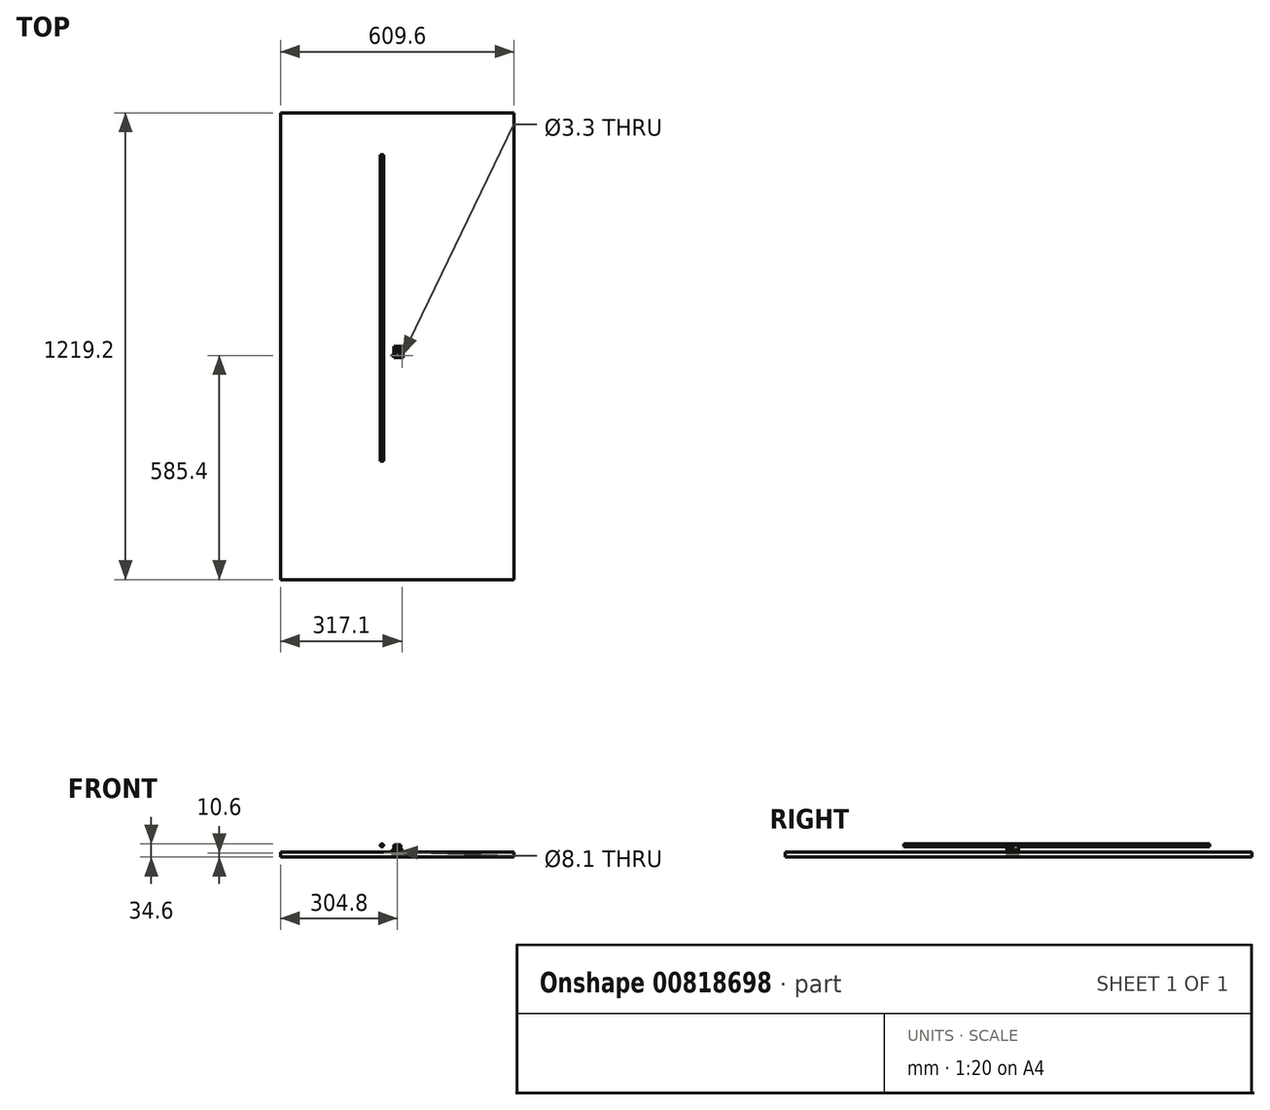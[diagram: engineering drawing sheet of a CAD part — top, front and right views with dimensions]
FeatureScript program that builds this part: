
annotation { "Feature Type Name" : "Feature", "Feature Type Description" : "" }
export const myFeature = defineFeature(function(context is Context, id is Id, definition is map)
    precondition{}
    {
        {
            var Q0;
            Q0=qCreatedBy(makeId("Front.planeOp"),FACE);
            var sketch = newSketch(context, id + "F0", { "sketchPlane" : qUnion([Q0])});
            skLineSegment(sketch, "E0", {"start": v(-20.5, 0) * mm, "end": v(-20.5, 6) * mm});
            skLineSegment(sketch, "E1", {"start": v(-20.5, 6) * mm, "end": v(-8.95, 6) * mm});
            skLineSegment(sketch, "E2", {"start": v(-8.95, 6) * mm, "end": v(-8.95, 32) * mm});
            skLineSegment(sketch, "E3", {"start": v(-8.95, 32) * mm, "end": v(-0.65, 32) * mm});
            skLineSegment(sketch, "E4", {"start": v(-20.5, 0) * mm, "end": v(0, 0) * mm});
            skLineSegment(sketch, "E5.MirrorCS", {"start": v(8.95, 32) * mm, "end": v(0.65, 32) * mm});
            skLineSegment(sketch, "E6.MirrorCS", {"start": v(8.95, 6) * mm, "end": v(8.95, 32) * mm});
            skLineSegment(sketch, "E7.MirrorCS", {"start": v(20.5, 6) * mm, "end": v(8.95, 6) * mm});
            skLineSegment(sketch, "E8.MirrorCS", {"start": v(20.5, 0) * mm, "end": v(20.5, 6) * mm});
            skLineSegment(sketch, "E9.MirrorCS", {"start": v(20.5, 0) * mm, "end": v(0, 0) * mm});
            skArc(sketch, "E10", {"start": v(-0.65, 23.05) * mm, "mid": v(0, 14.9) * mm, "end": v(0.65, 23.05) * mm});
            skLineSegment(sketch, "E11", {"start": v(-0.65, 32) * mm, "end": v(-0.65, 23.05) * mm});
            skLineSegment(sketch, "E12.MirrorCS", {"start": v(0.65, 32) * mm, "end": v(0.65, 23.05) * mm});
            skPoint(sketch, "E13.orphan", {"position": v(0, 32) * mm});
            skSolve(sketch);
        }
        {
            var Q0;
            Q0=makeQuery(id+"F0.imprint","IMPRINT",FACE,{"disambiguationData":[TD([[makeQuery(id+"F0.imprint","IMPRINT",EDGE,{"derivedFrom":sQuery(id+"F0.wireOp",EDGE,"E0")}),-1.0]])]});
            extrude(context, id + "F1", {"entities" : qUnion([Q0]), "depth" : 14.5 * mm, "offsetDistance" : 25 * mm});
        }
        {
            var Q0;
            Q0=makeQuery(id+"F1.opExtrude","SWEPT_FACE",FACE,{"disambiguationData":[OSD([sQuery(id+"F0.wireOp",EDGE,"E4"),sQuery(id+"F0.wireOp",EDGE,"E9.MirrorCS")])]});
            var sketch = newSketch(context, id + "F2", { "sketchPlane" : qUnion([Q0])});
            skLineSegment(sketch, "E14", {"start": v(-20.5, 7.25) * mm, "end": v(20.5, 7.25) * mm, "construction": true});
            skCircle(sketch, "E15", {"center": v(-16, 7.25) * mm, "radius": 2.7 * mm});
            skCircle(sketch, "E16.MirrorC", {"center": v(16, 7.25) * mm, "radius": 2.7 * mm});
            skSolve(sketch);
        }
        {
            var Q0;
            Q0=makeQuery(id+"F2.imprint","IMPRINT",FACE,{"disambiguationData":[TD([[makeQuery(id+"F2.imprint","IMPRINT",EDGE,{"derivedFrom":sQuery(id+"F2.wireOp",EDGE,"E15")}),1.0]])]});
            var Q1;
            Q1=makeQuery(id+"F2.imprint","IMPRINT",FACE,{"disambiguationData":[TD([[makeQuery(id+"F2.imprint","IMPRINT",EDGE,{"derivedFrom":sQuery(id+"F2.wireOp",EDGE,"E16.MirrorC")}),-1.0]])]});
            var Q2;
            Q2=makeQuery(id+"F1.opExtrude","SWEPT_FACE",FACE,{"disambiguationData":[OSD([sQuery(id+"F0.wireOp",EDGE,"E1")])]});
            extrude(context, id + "F3", {"entities" : qUnion([Q0, Q1]), "operationType" : NewBodyOperationType.REMOVE, "endBound" : BoundingType.UP_TO_SURFACE, "oppositeDirection" : true, "depth" : 25 * mm, "endBoundEntityFace" : qUnion([Q2]), "offsetDistance" : 25 * mm});
        }
        {
            var Q0;
            Q0=qCreatedBy(makeId("Front.planeOp"),FACE);
            var sketch = newSketch(context, id + "F4", { "sketchPlane" : qUnion([Q0])});
            skCircle(sketch, "E17", {"center": v(-40, 30) * mm, "radius": 4 * mm});
            skSolve(sketch);
        }
        {
            var Q0;
            Q0=makeQuery(id+"F4.imprint","IMPRINT",FACE,{"disambiguationData":[TD([[makeQuery(id+"F4.imprint","IMPRINT",EDGE,{"derivedFrom":sQuery(id+"F4.wireOp",EDGE,"E17")}),1.0]])]});
            extrude(context, id + "F5", {"entities" : qUnion([Q0]), "depth" : 300 * mm, "offsetDistance" : 25 * mm});
        }
        {
            var Q0;
            Q0=makeQuery(id+"F4.imprint","IMPRINT",FACE,{"disambiguationData":[TD([[makeQuery(id+"F4.imprint","IMPRINT",EDGE,{"derivedFrom":sQuery(id+"F4.wireOp",EDGE,"E17")}),1.0]])]});
            extrude(context, id + "F6", {"entities" : qUnion([Q0]), "oppositeDirection" : true, "depth" : 500 * mm, "offsetDistance" : 25 * mm});
        }
        {
            var Q0;
            Q0=qCreatedBy(makeId("Front.planeOp"),FACE);
            var sketch = newSketch(context, id + "F7", { "sketchPlane" : qUnion([Q0])});
            skLineSegment(sketch, "E18", {"start": v(0, 0) * mm, "end": v(-6.5, 0) * mm});
            skLineSegment(sketch, "E19", {"start": v(-6.5, 0) * mm, "end": v(-6.5, -0.6) * mm});
            skLineSegment(sketch, "E20", {"start": v(-6.5, -0.6) * mm, "end": v(-17, -0.6) * mm});
            skLineSegment(sketch, "E21", {"start": v(-17, -0.6) * mm, "end": v(-17, 6) * mm});
            skLineSegment(sketch, "E22", {"start": v(-17, 6) * mm, "end": v(-15.5, 7.4) * mm});
            skLineSegment(sketch, "E23", {"start": v(-15.5, 7.4) * mm, "end": v(-15.5, 17.4) * mm});
            skLineSegment(sketch, "E24", {"start": v(-5, 21) * mm, "end": v(0, 21) * mm});
            skCircle(sketch, "E25", {"center": v(0, 10) * mm, "radius": 4.05 * mm});
            skCircle(sketch, "E26", {"center": v(0, 10) * mm, "radius": 7.5 * mm});
            skLineSegment(sketch, "E27", {"start": v(-15.5, 17.4) * mm, "end": v(-8.5, 17.4) * mm});
            skLineSegment(sketch, "E28", {"start": v(-8.5, 17.4) * mm, "end": v(-5, 21) * mm});
            skLineSegment(sketch, "E29.MirrorCS", {"start": v(5, 21) * mm, "end": v(0, 21) * mm});
            skLineSegment(sketch, "E30.MirrorCS", {"start": v(8.5, 17.4) * mm, "end": v(5, 21) * mm});
            skLineSegment(sketch, "E31.MirrorCS", {"start": v(15.5, 17.4) * mm, "end": v(8.5, 17.4) * mm});
            skLineSegment(sketch, "E32.MirrorCS", {"start": v(15.5, 7.4) * mm, "end": v(15.5, 17.4) * mm});
            skLineSegment(sketch, "E33.MirrorCS", {"start": v(17, 6) * mm, "end": v(15.5, 7.4) * mm});
            skLineSegment(sketch, "E34.MirrorCS", {"start": v(17, -0.6) * mm, "end": v(17, 6) * mm});
            skLineSegment(sketch, "E35.MirrorCS", {"start": v(6.5, -0.6) * mm, "end": v(17, -0.6) * mm});
            skLineSegment(sketch, "E36.MirrorCS", {"start": v(0, 0) * mm, "end": v(6.5, 0) * mm});
            skLineSegment(sketch, "E37.MirrorCS", {"start": v(6.5, 0) * mm, "end": v(6.5, -0.6) * mm});
            skSolve(sketch);
        }
        {
            var Q0;
            Q0=makeQuery(id+"F7.imprint","IMPRINT",FACE,{"disambiguationData":[TD([[makeQuery(id+"F7.imprint","IMPRINT",EDGE,{"derivedFrom":sQuery(id+"F7.wireOp",EDGE,"E18")}),-1.0]])]});
            var Q1;
            Q1=makeQuery(id+"F7.imprint","IMPRINT",FACE,{"disambiguationData":[TD([[makeQuery(id+"F7.imprint","IMPRINT",EDGE,{"derivedFrom":sQuery(id+"F7.wireOp",EDGE,"E25")}),-1.0]])]});
            extrude(context, id + "F8", {"entities" : qUnion([Q0, Q1]), "depth" : 30 * mm, "offsetDistance" : 25 * mm});
        }
        {
            var Q0;
            Q0=makeQuery(id+"F8.opExtrude","SWEPT_FACE",FACE,{"disambiguationData":[OSD([sQuery(id+"F7.wireOp",EDGE,"E20")])]});
            var sketch = newSketch(context, id + "F9", { "sketchPlane" : qUnion([Q0])});
            skLineSegment(sketch, "E38", {"start": v(-17, 5.8) * mm, "end": v(17, 5.8) * mm, "construction": true});
            skCircle(sketch, "E39", {"center": v(-12.3, 5.8) * mm, "radius": 1.65 * mm});
            skLineSegment(sketch, "E40", {"start": v(-17, 15) * mm, "end": v(17, 15) * mm, "construction": true});
            skCircle(sketch, "E41.MirrorC", {"center": v(-12.3, 24.2) * mm, "radius": 1.65 * mm});
            skCircle(sketch, "E42.MirrorC", {"center": v(12.3, 24.2) * mm, "radius": 1.65 * mm});
            skCircle(sketch, "E43.MirrorC", {"center": v(12.3, 5.8) * mm, "radius": 1.65 * mm});
            skLineSegment(sketch, "E44", {"start": v(-17, 30) * mm, "end": v(17, 0) * mm, "construction": true});
            skLineSegment(sketch, "E45", {"start": v(-17, 0) * mm, "end": v(17, 30) * mm, "construction": true});
            skPoint(sketch, "E46.0", {"position": v(17, 0) * mm});
            skPoint(sketch, "E47", {"position": v(0, 15) * mm});
            skSolve(sketch);
        }
        {
            var Q0;
            Q0=makeQuery(id+"F9.imprint","IMPRINT",FACE,{"disambiguationData":[TD([[makeQuery(id+"F9.imprint","IMPRINT",EDGE,{"derivedFrom":sQuery(id+"F9.wireOp",EDGE,"E41.MirrorC")}),-1.0]])]});
            var Q1;
            Q1=makeQuery(id+"F9.imprint","IMPRINT",FACE,{"disambiguationData":[TD([[makeQuery(id+"F9.imprint","IMPRINT",EDGE,{"derivedFrom":sQuery(id+"F9.wireOp",EDGE,"E39")}),1.0]])]});
            var Q2;
            Q2=makeQuery(id+"F9.imprint","IMPRINT",FACE,{"disambiguationData":[TD([[makeQuery(id+"F9.imprint","IMPRINT",EDGE,{"derivedFrom":sQuery(id+"F9.wireOp",EDGE,"E43.MirrorC")}),-1.0]])]});
            var Q3;
            Q3=makeQuery(id+"F9.imprint","IMPRINT",FACE,{"disambiguationData":[TD([[makeQuery(id+"F9.imprint","IMPRINT",EDGE,{"derivedFrom":sQuery(id+"F9.wireOp",EDGE,"E42.MirrorC")}),1.0]])]});
            var Q4;
            Q4=makeQuery(id+"F8.opExtrude","SWEPT_FACE",FACE,{"disambiguationData":[OSD([sQuery(id+"F7.wireOp",EDGE,"E27")])]});
            extrude(context, id + "F10", {"entities" : qUnion([Q0, Q1, Q2, Q3]), "operationType" : NewBodyOperationType.REMOVE, "endBound" : BoundingType.UP_TO_SURFACE, "oppositeDirection" : true, "depth" : 25 * mm, "endBoundEntityFace" : qUnion([Q4]), "offsetDistance" : 25 * mm});
        }
        {
            var Q0;
            Q0=makeQuery(id+"F7.imprint","IMPRINT",FACE,{"disambiguationData":[TD([[makeQuery(id+"F7.imprint","IMPRINT",EDGE,{"derivedFrom":sQuery(id+"F7.wireOp",EDGE,"E25")}),-1.0]])]});
            extrude(context, id + "F11", {"entities" : qUnion([Q0]), "operationType" : NewBodyOperationType.REMOVE, "depth" : 1 * mm, "offsetDistance" : 25 * mm});
        }
        {
            var Q0;
            Q0=makeQuery(id+"F8.opExtrude","CAP_FACE",FACE,{"disambiguationData":[OSD([sQuery(id+"F7.wireOp",EDGE,"E18"),sQuery(id+"F7.wireOp",EDGE,"E19"),sQuery(id+"F7.wireOp",EDGE,"E20"),sQuery(id+"F7.wireOp",EDGE,"E21"),sQuery(id+"F7.wireOp",EDGE,"E22"),sQuery(id+"F7.wireOp",EDGE,"E23"),sQuery(id+"F7.wireOp",EDGE,"E24"),sQuery(id+"F7.wireOp",EDGE,"E25"),sQuery(id+"F7.wireOp",EDGE,"E27"),sQuery(id+"F7.wireOp",EDGE,"E28"),sQuery(id+"F7.wireOp",EDGE,"E29.MirrorCS"),sQuery(id+"F7.wireOp",EDGE,"E30.MirrorCS"),sQuery(id+"F7.wireOp",EDGE,"E31.MirrorCS"),sQuery(id+"F7.wireOp",EDGE,"E32.MirrorCS"),sQuery(id+"F7.wireOp",EDGE,"E33.MirrorCS"),sQuery(id+"F7.wireOp",EDGE,"E34.MirrorCS"),sQuery(id+"F7.wireOp",EDGE,"E35.MirrorCS"),sQuery(id+"F7.wireOp",EDGE,"E36.MirrorCS"),sQuery(id+"F7.wireOp",EDGE,"E37.MirrorCS")])],"isStart":false});
            var sketch = newSketch(context, id + "F12", { "sketchPlane" : qUnion([Q0])});
            skCircle(sketch, "E48", {"center": v(0, 10) * mm, "radius": 7.5 * mm});
            skCircle(sketch, "E49", {"center": v(0, 10) * mm, "radius": 4.05 * mm});
            skSolve(sketch);
        }
        {
            var Q0;
            Q0=makeQuery(id+"F12.imprint","IMPRINT",FACE,{"disambiguationData":[TD([[makeQuery(id+"F12.imprint","IMPRINT",EDGE,{"derivedFrom":sQuery(id+"F12.wireOp",EDGE,"E48")}),1.0]])]});
            extrude(context, id + "F13", {"entities" : qUnion([Q0]), "operationType" : NewBodyOperationType.REMOVE, "oppositeDirection" : true, "depth" : 1 * mm, "offsetDistance" : 25 * mm});
        }
        {
            var Q0;
            Q0=qCreatedBy(makeId("Top.planeOp"),FACE);
            var sketch = newSketch(context, id + "F14", { "sketchPlane" : qUnion([Q0])});
            skLineSegment(sketch, "E50.bottom", {"start": v(304.8, 609.6) * mm, "end": v(-304.8, 609.6) * mm});
            skLineSegment(sketch, "E50.top", {"start": v(304.8, -609.6) * mm, "end": v(-304.8, -609.6) * mm});
            skLineSegment(sketch, "E50.left", {"start": v(304.8, 609.6) * mm, "end": v(304.8, -609.6) * mm});
            skLineSegment(sketch, "E50.right", {"start": v(-304.8, 609.6) * mm, "end": v(-304.8, -609.6) * mm});
            skPoint(sketch, "E50.middle", {"position": v(0, 0) * mm});
            skSolve(sketch);
        }
        {
            var Q0;
            Q0=makeQuery(id+"F14.imprint","IMPRINT",FACE,{"disambiguationData":[TD([[makeQuery(id+"F14.imprint","IMPRINT",EDGE,{"derivedFrom":sQuery(id+"F14.wireOp",EDGE,"E50.bottom")}),1.0]])]});
            extrude(context, id + "F15", {"entities" : qUnion([Q0]), "depth" : 12.6 * mm, "offsetDistance" : 25 * mm});
        }
    });
